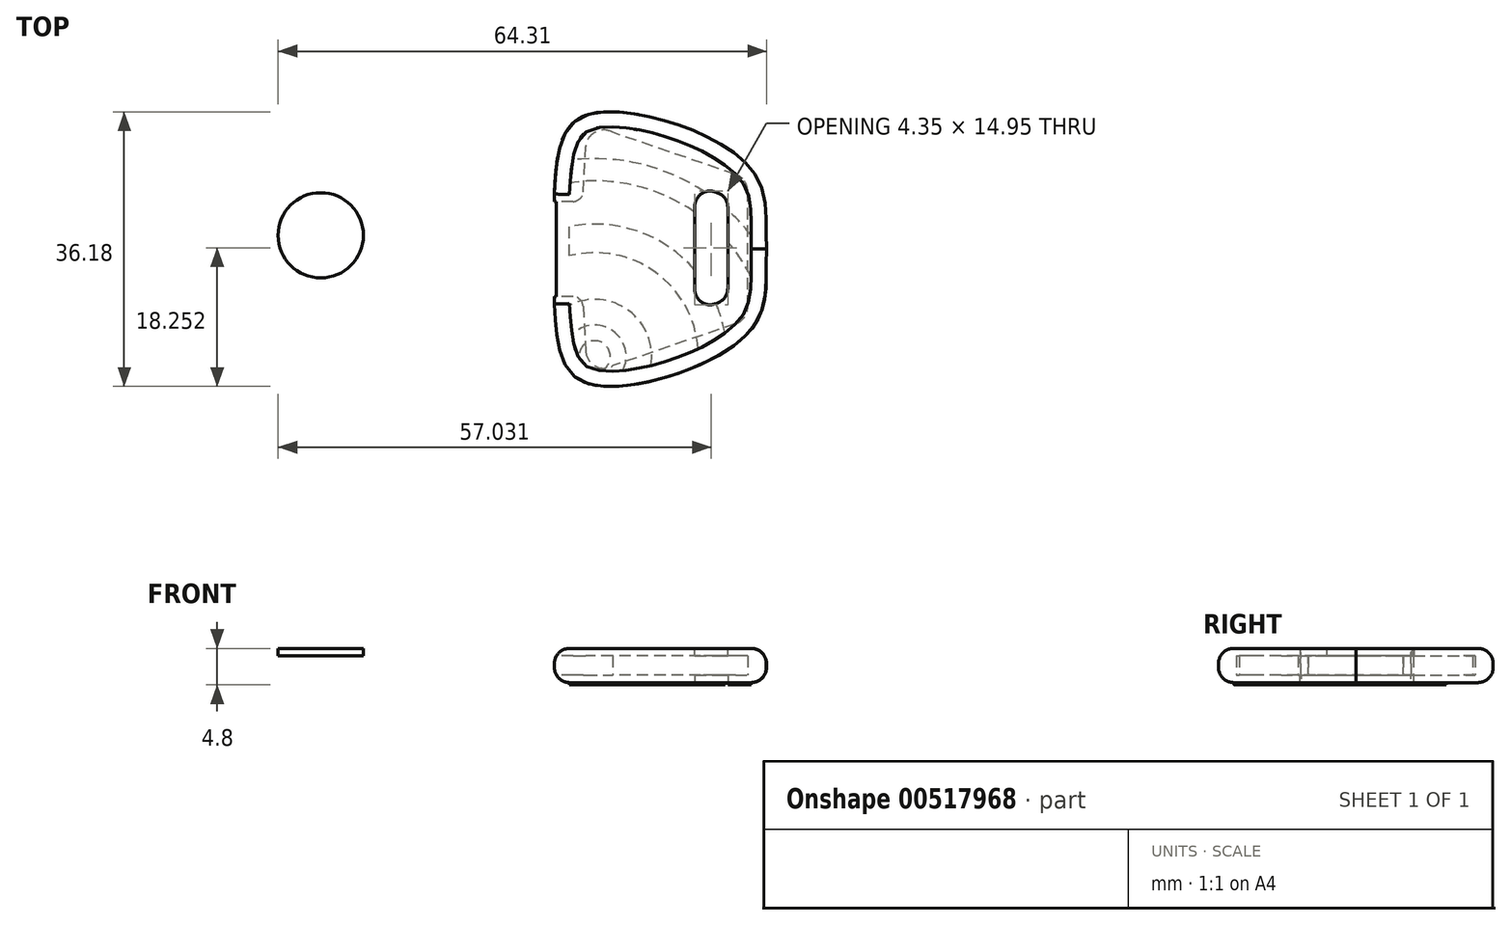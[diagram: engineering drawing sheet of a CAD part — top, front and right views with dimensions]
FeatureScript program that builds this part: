
annotation { "Feature Type Name" : "Feature", "Feature Type Description" : "" }
export const myFeature = defineFeature(function(context is Context, id is Id, definition is map)
    precondition{}
    {
        {
            var Q0;
            Q0=qCreatedBy(makeId("Top.planeOp"),FACE);
            var sketch = newSketch(context, id + "F0", { "sketchPlane" : qUnion([Q0])});
            skPoint(sketch, "E0", {"position": v(-41.2, -25.62) * mm});
            skPoint(sketch, "E1", {"position": v(-31.2, -25.62) * mm});
            skPoint(sketch, "E2", {"position": v(11.52, 6.21) * mm});
            skPoint(sketch, "E3", {"position": v(11.52, -6.54) * mm});
            skLineSegment(sketch, "E4", {"start": v(0, 15.95) * mm, "end": v(0, -17.25) * mm, "construction": true});
            skLineSegment(sketch, "E5", {"start": v(0, 0) * mm, "end": v(43.28, 0) * mm, "construction": true});
            skFitSpline(sketch, "E6", {"points": [v(0, 7.25) * mm, v(5.72, 18) * mm, v(26.02, 10.45) * mm, v(27.94, 0) * mm], "startDerivative": vector(2.6, 71.25) * mm, "endDerivative": vector(2.73, -33.65) * mm});
            skPoint(sketch, "E7", {"position": v(24.94, 0) * mm});
            skFitSpline(sketch, "E8.MirrorCS", {"points": [v(0, -7.25) * mm, v(5.72, -18) * mm, v(26.02, -10.45) * mm, v(27.94, 0) * mm], "startDerivative": vector(2.6, -71.25) * mm, "endDerivative": vector(2.73, 33.65) * mm});
            skLineSegment(sketch, "E9", {"start": v(0, 7.25) * mm, "end": v(0, -7.25) * mm});
            skLineSegment(sketch, "E10", {"start": v(0, 5.77) * mm, "end": v(2.46, 5.77) * mm, "construction": true});
            skLineSegment(sketch, "E11", {"start": v(4.63, 13.45) * mm, "end": v(4.28, 7.5) * mm, "construction": true});
            skLineSegment(sketch, "E12", {"start": v(7.51, 14.9) * mm, "end": v(23.7, 9.35) * mm, "construction": true});
            skLineSegment(sketch, "E13", {"start": v(24.94, 7.58) * mm, "end": v(24.94, 0) * mm, "construction": true});
            skFitSpline(sketch, "E14", {"points": [v(23.7, 9.35) * mm, v(24.57, 8.68) * mm, v(24.94, 7.58) * mm], "startDerivative": vector(1.84, -0.6) * mm, "endDerivative": vector(0.19, -3.28) * mm, "construction": true});
            skFitSpline(sketch, "E15", {"points": [v(4.63, 13.45) * mm, v(5.65, 14.77) * mm, v(7.51, 14.9) * mm], "startDerivative": vector(1.36, 4.9) * mm, "endDerivative": vector(4.54, -1.86) * mm, "construction": true});
            skFitSpline(sketch, "E16", {"points": [v(2.46, 5.77) * mm, v(3.74, 6.04) * mm, v(4.28, 7.5) * mm], "startDerivative": vector(3.45, -0.17) * mm, "endDerivative": vector(-0.2, 4.31) * mm, "construction": true});
            skLineSegment(sketch, "E17", {"start": v(0, 6.27) * mm, "end": v(2.45, 6.27) * mm});
            skLineSegment(sketch, "E18", {"start": v(4.14, 13.48) * mm, "end": v(3.78, 7.52) * mm});
            skLineSegment(sketch, "E19", {"start": v(7.68, 15.37) * mm, "end": v(23.85, 9.83) * mm});
            skLineSegment(sketch, "E20", {"start": v(25.44, 7.58) * mm, "end": v(25.44, 0) * mm});
            skLineSegment(sketch, "E21", {"start": v(3.78, 7.52) * mm, "end": v(4.28, 7.5) * mm, "construction": true});
            skLineSegment(sketch, "E22", {"start": v(4.14, 13.48) * mm, "end": v(4.63, 13.45) * mm, "construction": true});
            skLineSegment(sketch, "E23", {"start": v(7.68, 15.37) * mm, "end": v(7.51, 14.9) * mm, "construction": true});
            skLineSegment(sketch, "E24", {"start": v(23.85, 9.83) * mm, "end": v(23.7, 9.35) * mm, "construction": true});
            skLineSegment(sketch, "E25", {"start": v(24.94, 7.58) * mm, "end": v(25.44, 7.58) * mm, "construction": true});
            skLineSegment(sketch, "E26", {"start": v(25.44, 0) * mm, "end": v(24.94, 0) * mm, "construction": true});
            skArc(sketch, "E27", {"start": v(2.45, 6.27) * mm, "mid": v(3.37, 6.63) * mm, "end": v(3.78, 7.52) * mm});
            skArc(sketch, "E28", {"start": v(7.68, 15.37) * mm, "mid": v(5.38, 15.41) * mm, "end": v(4.14, 13.48) * mm});
            skArc(sketch, "E29", {"start": v(25.44, 7.58) * mm, "mid": v(25.01, 8.96) * mm, "end": v(23.85, 9.83) * mm});
            skLineSegment(sketch, "E30.MirrorCS", {"start": v(25.44, -7.58) * mm, "end": v(25.44, 0) * mm});
            skArc(sketch, "E31.MirrorCS", {"start": v(25.44, -7.58) * mm, "mid": v(25.01, -8.96) * mm, "end": v(23.85, -9.83) * mm});
            skLineSegment(sketch, "E32.MirrorCS", {"start": v(7.68, -15.37) * mm, "end": v(23.85, -9.83) * mm});
            skArc(sketch, "E33.MirrorCS", {"start": v(7.68, -15.37) * mm, "mid": v(5.38, -15.41) * mm, "end": v(4.14, -13.48) * mm});
            skLineSegment(sketch, "E34.MirrorCS", {"start": v(0, -6.27) * mm, "end": v(2.45, -6.27) * mm});
            skLineSegment(sketch, "E35.MirrorCS", {"start": v(4.14, -13.48) * mm, "end": v(3.78, -7.52) * mm});
            skArc(sketch, "E36.MirrorCS", {"start": v(2.45, -6.27) * mm, "mid": v(3.37, -6.63) * mm, "end": v(3.78, -7.52) * mm});
            skLineSegment(sketch, "E37", {"start": v(18.49, 8.45) * mm, "end": v(18.49, -8.2) * mm});
            skLineSegment(sketch, "E38", {"start": v(18.49, -8.2) * mm, "end": v(22.83, -6.59) * mm});
            skLineSegment(sketch, "E39", {"start": v(22.83, -6.59) * mm, "end": v(22.83, 6.95) * mm});
            skLineSegment(sketch, "E40", {"start": v(22.83, 6.95) * mm, "end": v(18.49, 8.45) * mm});
            skLineSegment(sketch, "E41", {"start": v(19.09, 8.87) * mm, "end": v(22.03, 7.87) * mm, "construction": true});
            skLineSegment(sketch, "E42", {"start": v(17.8, 7.95) * mm, "end": v(17.8, -7.49) * mm, "construction": true});
            skLineSegment(sketch, "E43", {"start": v(18.89, -8.8) * mm, "end": v(22.02, -7.64) * mm, "construction": true});
            skLineSegment(sketch, "E44", {"start": v(23.06, -6.3) * mm, "end": v(23.06, 6.7) * mm, "construction": true});
            skLineSegment(sketch, "E45", {"start": v(22.03, 7.87) * mm, "end": v(23.06, 6.7) * mm});
            skLineSegment(sketch, "E46", {"start": v(23.06, -6.3) * mm, "end": v(22.02, -7.64) * mm});
            skLineSegment(sketch, "E47", {"start": v(18.89, -8.8) * mm, "end": v(17.8, -7.49) * mm});
            skLineSegment(sketch, "E48", {"start": v(17.8, 7.95) * mm, "end": v(19.09, 8.87) * mm});
            skCircle(sketch, "E49", {"center": v(-30.76, 1.81) * mm, "radius": 5.61 * mm});
            skSolve(sketch);
        }
        {
            var Q0;
            {var subQ1=sQuery(id+"F0.wireOp",EDGE,"E6");Q0=makeQuery(id+"F0.imprint","IMPRINT",FACE,{"disambiguationData":[TD([[makeQuery(id+"F0.imprint","IMPRINT",EDGE,{"derivedFrom":subQ1}),-1.0]])]});}
            var Q1;
            {var subQ0=sQuery(id+"F0.wireOp",EDGE,"E17");Q1=makeQuery(id+"F0.imprint","IMPRINT",FACE,{"disambiguationData":[TD([[makeQuery(id+"F0.imprint","IMPRINT",EDGE,{"derivedFrom":subQ0}),-1.0]])]});}
            var Q2;
            Q2=makeQuery(id+"F0.imprint","IMPRINT",FACE,{"disambiguationData":[TD([[makeQuery(id+"F0.imprint","IMPRINT",EDGE,{"derivedFrom":sQuery(id+"F0.wireOp",EDGE,"E49")}),1.0]])]});
            var Q3;
            Q3=sQuery(id+"F0.wireOp",EDGE,"E6");
            var Q4;
            Q4=sQuery(id+"F0.wireOp",EDGE,"E9");
            var Q5;
            Q5=sQuery(id+"F0.wireOp",EDGE,"E8.MirrorCS");
            extrude(context, id + "F1", {"entities" : qUnion([Q0, Q1, Q2]), "surfaceEntities" : qUnion([Q3, Q4, Q5]), "depth" : 1 * mm, "offsetDistance" : 25 * mm});
        }
        {
            var Q0;
            {var subQ1=sQuery(id+"F0.wireOp",EDGE,"E6");Q0=makeQuery(id+"F0.imprint","IMPRINT",FACE,{"disambiguationData":[TD([[makeQuery(id+"F0.imprint","IMPRINT",EDGE,{"derivedFrom":subQ1}),-1.0]])]});}
            extrude(context, id + "F2", {"entities" : qUnion([Q0]), "operationType" : NewBodyOperationType.ADD, "depth" : ((2 + 2.5) / 2) * mm, "offsetDistance" : 25 * mm});
        }
        {
            var Q0;
            Q0=makeQuery(id+"F2.opExtrude","CAP_FACE",FACE,{"disambiguationData":[OSD([sQuery(id+"F0.wireOp",EDGE,"E6"),sQuery(id+"F0.wireOp",EDGE,"E8.MirrorCS"),sQuery(id+"F0.wireOp",EDGE,"E9"),sQuery(id+"F0.wireOp",EDGE,"E17"),sQuery(id+"F0.wireOp",EDGE,"E18"),sQuery(id+"F0.wireOp",EDGE,"E19"),sQuery(id+"F0.wireOp",EDGE,"E20"),sQuery(id+"F0.wireOp",EDGE,"E27"),sQuery(id+"F0.wireOp",EDGE,"E28"),sQuery(id+"F0.wireOp",EDGE,"E29"),sQuery(id+"F0.wireOp",EDGE,"E30.MirrorCS"),sQuery(id+"F0.wireOp",EDGE,"E31.MirrorCS"),sQuery(id+"F0.wireOp",EDGE,"E32.MirrorCS"),sQuery(id+"F0.wireOp",EDGE,"E33.MirrorCS"),sQuery(id+"F0.wireOp",EDGE,"E34.MirrorCS"),sQuery(id+"F0.wireOp",EDGE,"E35.MirrorCS"),sQuery(id+"F0.wireOp",EDGE,"E36.MirrorCS")])],"isStart":false});
            cPlane(context, id + "F3", {"entities" : qUnion([Q0]), "cplaneType" : CPlaneType.OFFSET, "offset" : 0 * mm, "width" : 150 * mm, "height" : 150 * mm});
        }
        {
            var Q0;
            Q0=makeQuery(id+"F1.opExtrude","SWEPT_BODY",BODY,{"disambiguationData":[OSD([sQuery(id+"F0.wireOp",EDGE,"E6"),sQuery(id+"F0.wireOp",EDGE,"E8.MirrorCS"),sQuery(id+"F0.wireOp",EDGE,"E9"),sQuery(id+"F0.wireOp",EDGE,"VUIZ95Wj-6tOB-U0YA-8sAB-wQhS3JJIxJTj"),sQuery(id+"F0.wireOp",EDGE,"eSFFgtQ0-YFcI-sS7r-1Ndp-ZKPIy7ymWjVM"),sQuery(id+"F0.wireOp",EDGE,"eviLKCoZ-uwRQ-ZiHB-HchL-FsuIOfkkec4v"),sQuery(id+"F0.wireOp",EDGE,"iIHeamZd-nrCs-mJiL-hRhE-kadTkk34Sg0T")])]});
            var Q1;
            Q1=makeQuery(id+"F1.opExtrude","SWEPT_BODY",BODY,{"disambiguationData":[OSD([sQuery(id+"F0.wireOp",EDGE,"E49")])]});
            var Q2;
            Q2=qCreatedBy(id+"F3.planeOp",FACE);
            mirror(context, id + "F4", {"operationType" : NewBodyOperationType.ADD, "entities" : qUnion([Q0, Q1]), "mirrorPlane" : qUnion([Q2])});
        }
        {
            var Q0;
            Q0=makeQuery(id+"F4.opPattern","COPY",EDGE,{"derivedFrom":makeQuery(id+"F1.opExtrude","CAP_EDGE",EDGE,{"disambiguationData":[OSD([sQuery(id+"F0.wireOp",EDGE,"E6")])],"isStart":true}),"instanceName":"1"});
            var Q1;
            Q1=makeQuery(id+"F1.opExtrude","CAP_EDGE",EDGE,{"disambiguationData":[OSD([sQuery(id+"F0.wireOp",EDGE,"E6")])],"isStart":true});
            var Q2;
            Q2=makeQuery(id+"F4.opPattern","COPY",EDGE,{"derivedFrom":makeQuery(id+"F1.opExtrude","CAP_EDGE",EDGE,{"disambiguationData":[OSD([sQuery(id+"F0.wireOp",EDGE,"E8.MirrorCS")])],"isStart":true}),"instanceName":"1"});
            var Q3;
            Q3=makeQuery(id+"F1.opExtrude","CAP_EDGE",EDGE,{"disambiguationData":[OSD([sQuery(id+"F0.wireOp",EDGE,"E8.MirrorCS")])],"isStart":true});
            fillet(context, id + "F5", {"entities" : qUnion([Q0, Q1, Q2, Q3]), "radius" : 2 * mm, "tangentPropagation" : true, "allowEdgeOverflow" : false});
        }
        {
            var Q0;
            Q0=makeQuery(id+"F4.opPattern","COPY",EDGE,{"derivedFrom":makeQuery(id+"F1.opExtrude","SWEPT_EDGE",EDGE,{"disambiguationData":[OSD([sQuery(id+"F0.wireOp",EDGE,"E39"),sQuery(id+"F0.wireOp",EDGE,"E40")])]}),"instanceName":"1"});
            var Q1;
            Q1=makeQuery(id+"F1.opExtrude","SWEPT_EDGE",EDGE,{"disambiguationData":[OSD([sQuery(id+"F0.wireOp",EDGE,"E39"),sQuery(id+"F0.wireOp",EDGE,"E40")])]});
            var Q2;
            Q2=makeQuery(id+"F1.opExtrude","SWEPT_EDGE",EDGE,{"disambiguationData":[OSD([sQuery(id+"F0.wireOp",EDGE,"E37"),sQuery(id+"F0.wireOp",EDGE,"E40")])]});
            var Q3;
            Q3=makeQuery(id+"F4.opPattern","COPY",EDGE,{"derivedFrom":makeQuery(id+"F1.opExtrude","SWEPT_EDGE",EDGE,{"disambiguationData":[OSD([sQuery(id+"F0.wireOp",EDGE,"E37"),sQuery(id+"F0.wireOp",EDGE,"E40")])]}),"instanceName":"1"});
            var Q4;
            Q4=makeQuery(id+"F1.opExtrude","SWEPT_EDGE",EDGE,{"disambiguationData":[OSD([sQuery(id+"F0.wireOp",EDGE,"E38"),sQuery(id+"F0.wireOp",EDGE,"E39")])]});
            var Q5;
            Q5=makeQuery(id+"F4.opPattern","COPY",EDGE,{"derivedFrom":makeQuery(id+"F1.opExtrude","SWEPT_EDGE",EDGE,{"disambiguationData":[OSD([sQuery(id+"F0.wireOp",EDGE,"E38"),sQuery(id+"F0.wireOp",EDGE,"E39")])]}),"instanceName":"1"});
            var Q6;
            Q6=makeQuery(id+"F1.opExtrude","SWEPT_EDGE",EDGE,{"disambiguationData":[OSD([sQuery(id+"F0.wireOp",EDGE,"E37"),sQuery(id+"F0.wireOp",EDGE,"E38")])]});
            var Q7;
            Q7=makeQuery(id+"F4.opPattern","COPY",EDGE,{"derivedFrom":makeQuery(id+"F1.opExtrude","SWEPT_EDGE",EDGE,{"disambiguationData":[OSD([sQuery(id+"F0.wireOp",EDGE,"E37"),sQuery(id+"F0.wireOp",EDGE,"E38")])]}),"instanceName":"1"});
            fillet(context, id + "F6", {"entities" : qUnion([Q0, Q1, Q2, Q3, Q4, Q5, Q6, Q7]), "radius" : 2 * mm, "tangentPropagation" : true, "allowEdgeOverflow" : false});
        }
        {
            var Q0;
            Q0=makeQuery(id+"F1.opExtrude","CAP_FACE",FACE,{"disambiguationData":[OSD([sQuery(id+"F0.wireOp",EDGE,"E6"),sQuery(id+"F0.wireOp",EDGE,"E8.MirrorCS"),sQuery(id+"F0.wireOp",EDGE,"E9"),sQuery(id+"F0.wireOp",EDGE,"E37"),sQuery(id+"F0.wireOp",EDGE,"E38"),sQuery(id+"F0.wireOp",EDGE,"E39"),sQuery(id+"F0.wireOp",EDGE,"E40")])],"isStart":true});
            var sketch = newSketch(context, id + "F7", { "sketchPlane" : qUnion([Q0])});
            skCircle(sketch, "E50", {"center": v(5.3, 14.14) * mm, "radius": 2.07 * mm});
            skCircle(sketch, "E51", {"center": v(5.3, 14.14) * mm, "radius": 4.15 * mm});
            skCircle(sketch, "E52", {"center": v(5.3, 14.14) * mm, "radius": 7.51 * mm});
            skCircle(sketch, "E53", {"center": v(5.3, 14.14) * mm, "radius": 13.67 * mm});
            skCircle(sketch, "E54", {"center": v(5.3, 14.14) * mm, "radius": 17.42 * mm});
            skCircle(sketch, "E55", {"center": v(5.3, 14.14) * mm, "radius": 23.12 * mm});
            skCircle(sketch, "E56", {"center": v(5.3, 14.14) * mm, "radius": 26.05 * mm});
            skSolve(sketch);
        }
        {
            var Q0;
            {var subQ0=sQuery(id+"F0.wireOp",EDGE,"E38");var subQ1=sQuery(id+"F0.wireOp",EDGE,"E37");var subQ2=sQuery(id+"F0.wireOp",EDGE,"E8.MirrorCS");var subQ3=sQuery(id+"F0.wireOp",EDGE,"E6");var subQ4=makeQuery(id+"F1.opExtrude","CAP_FACE",FACE,{"disambiguationData":[OSD([subQ3,subQ2,sQuery(id+"F0.wireOp",EDGE,"E9"),subQ1,subQ0,sQuery(id+"F0.wireOp",EDGE,"E39"),sQuery(id+"F0.wireOp",EDGE,"E40")])],"isStart":true});var subQ5=makeQuery(id+"F6.opFillet","BLEND_EDGE",EDGE,{"blendedFrom":[makeQuery(id+"F1.opExtrude","SWEPT_EDGE",EDGE,{"disambiguationData":[OSD([subQ1,subQ0])]}),subQ4],"blendedInto":[subQ4]});Q0=makeQuery(id+"F7.imprint","IMPRINT",FACE,{"disambiguationData":[TD([[makeQuery(id+"F7.imprint","IMPRINT",EDGE,{"derivedFrom":subQ5}),1.0]])]});}
            var Q1;
            {var subQ0=sQuery(id+"F0.wireOp",EDGE,"E37");var subQ1=makeQuery(id+"F1.opExtrude","CAP_EDGE",EDGE,{"disambiguationData":[OSD([subQ0])],"isStart":true});var subQ11=sQuery(id+"F7.wireOp",EDGE,"E55");var subQ13=makeQuery(id+"F7.imprint","INTERSECT",VERTEX,{"derivedFrom":[subQ1,subQ11]});Q1=makeQuery(id+"F7.imprint","IMPRINT",FACE,{"disambiguationData":[TD([[makeQuery(id+"F7.imprint","IMPRINT",EDGE,{"disambiguationData":[TD([[subQ13,1.0]])],"derivedFrom":subQ11}),-1.0]])]});}
            var Q2;
            {var subQ0=sQuery(id+"F7.wireOp",EDGE,"E51");var subQ1=sQuery(id+"F0.wireOp",EDGE,"E8.MirrorCS");var subQ2=makeQuery(id+"F5.opFillet","BLEND_EDGE",EDGE,{"blendedFrom":[makeQuery(id+"F1.opExtrude","CAP_EDGE",EDGE,{"disambiguationData":[OSD([subQ1])],"isStart":true}),makeQuery(id+"F1.opExtrude","CAP_FACE",FACE,{"disambiguationData":[OSD([sQuery(id+"F0.wireOp",EDGE,"E6"),subQ1,sQuery(id+"F0.wireOp",EDGE,"E9"),sQuery(id+"F0.wireOp",EDGE,"E37"),sQuery(id+"F0.wireOp",EDGE,"E38"),sQuery(id+"F0.wireOp",EDGE,"E39"),sQuery(id+"F0.wireOp",EDGE,"E40")])],"isStart":true})],"blendedInto":[makeQuery(id+"F1.opExtrude","CAP_FACE",FACE,{"disambiguationData":[OSD([sQuery(id+"F0.wireOp",EDGE,"E6"),subQ1,sQuery(id+"F0.wireOp",EDGE,"E9"),sQuery(id+"F0.wireOp",EDGE,"E37"),sQuery(id+"F0.wireOp",EDGE,"E38"),sQuery(id+"F0.wireOp",EDGE,"E39"),sQuery(id+"F0.wireOp",EDGE,"E40")])],"isStart":true})]});var subQ3=makeQuery(id+"F7.imprint","INTERSECT",VERTEX,{"disambiguationData":[OD(0.0)],"derivedFrom":[subQ2,subQ0]});Q2=makeQuery(id+"F7.imprint","IMPRINT",FACE,{"disambiguationData":[TD([[makeQuery(id+"F7.imprint","IMPRINT",EDGE,{"disambiguationData":[TD([[subQ3,-1.0]])],"derivedFrom":subQ0}),-1.0]])]});}
            var Q3;
            {var subQ0=sQuery(id+"F0.wireOp",EDGE,"E39");var subQ9=makeQuery(id+"F1.opExtrude","CAP_EDGE",EDGE,{"disambiguationData":[OSD([subQ0])],"isStart":true});var subQ11=sQuery(id+"F7.wireOp",EDGE,"E55");var subQ13=makeQuery(id+"F7.imprint","INTERSECT",VERTEX,{"derivedFrom":[subQ9,subQ11]});Q3=makeQuery(id+"F7.imprint","IMPRINT",FACE,{"disambiguationData":[TD([[makeQuery(id+"F7.imprint","IMPRINT",EDGE,{"disambiguationData":[TD([[subQ13,-1.0]])],"derivedFrom":subQ9}),1.0]])]});}
            var Q4;
            {var subQ0=sQuery(id+"F7.wireOp",EDGE,"E50");var subQ1=sQuery(id+"F0.wireOp",EDGE,"E8.MirrorCS");var subQ2=makeQuery(id+"F5.opFillet","BLEND_EDGE",EDGE,{"blendedFrom":[makeQuery(id+"F1.opExtrude","CAP_EDGE",EDGE,{"disambiguationData":[OSD([subQ1])],"isStart":true}),makeQuery(id+"F1.opExtrude","CAP_FACE",FACE,{"disambiguationData":[OSD([sQuery(id+"F0.wireOp",EDGE,"E6"),subQ1,sQuery(id+"F0.wireOp",EDGE,"E9"),sQuery(id+"F0.wireOp",EDGE,"E37"),sQuery(id+"F0.wireOp",EDGE,"E38"),sQuery(id+"F0.wireOp",EDGE,"E39"),sQuery(id+"F0.wireOp",EDGE,"E40")])],"isStart":true})],"blendedInto":[makeQuery(id+"F1.opExtrude","CAP_FACE",FACE,{"disambiguationData":[OSD([sQuery(id+"F0.wireOp",EDGE,"E6"),subQ1,sQuery(id+"F0.wireOp",EDGE,"E9"),sQuery(id+"F0.wireOp",EDGE,"E37"),sQuery(id+"F0.wireOp",EDGE,"E38"),sQuery(id+"F0.wireOp",EDGE,"E39"),sQuery(id+"F0.wireOp",EDGE,"E40")])],"isStart":true})]});var subQ3=makeQuery(id+"F7.imprint","INTERSECT",VERTEX,{"disambiguationData":[OD(0.0)],"derivedFrom":[subQ2,subQ0]});Q4=makeQuery(id+"F7.imprint","IMPRINT",FACE,{"disambiguationData":[TD([[makeQuery(id+"F7.imprint","IMPRINT",EDGE,{"disambiguationData":[TD([[subQ3,-1.0]])],"derivedFrom":subQ0}),1.0]])]});}
            extrude(context, id + "F8", {"entities" : qUnion([Q0, Q1, Q2, Q3, Q4]), "operationType" : NewBodyOperationType.ADD, "depth" : 0.3 * mm, "offsetDistance" : 25 * mm});
        }
        {
            var Q0;
            Q0=makeQuery(id+"F1.opExtrude","SWEPT_BODY",BODY,{"disambiguationData":[OSD([sQuery(id+"F0.wireOp",EDGE,"E49")])]});
            deleteBodies(context, id + "F9", {"entities" : qUnion([Q0])});
        }
    });
